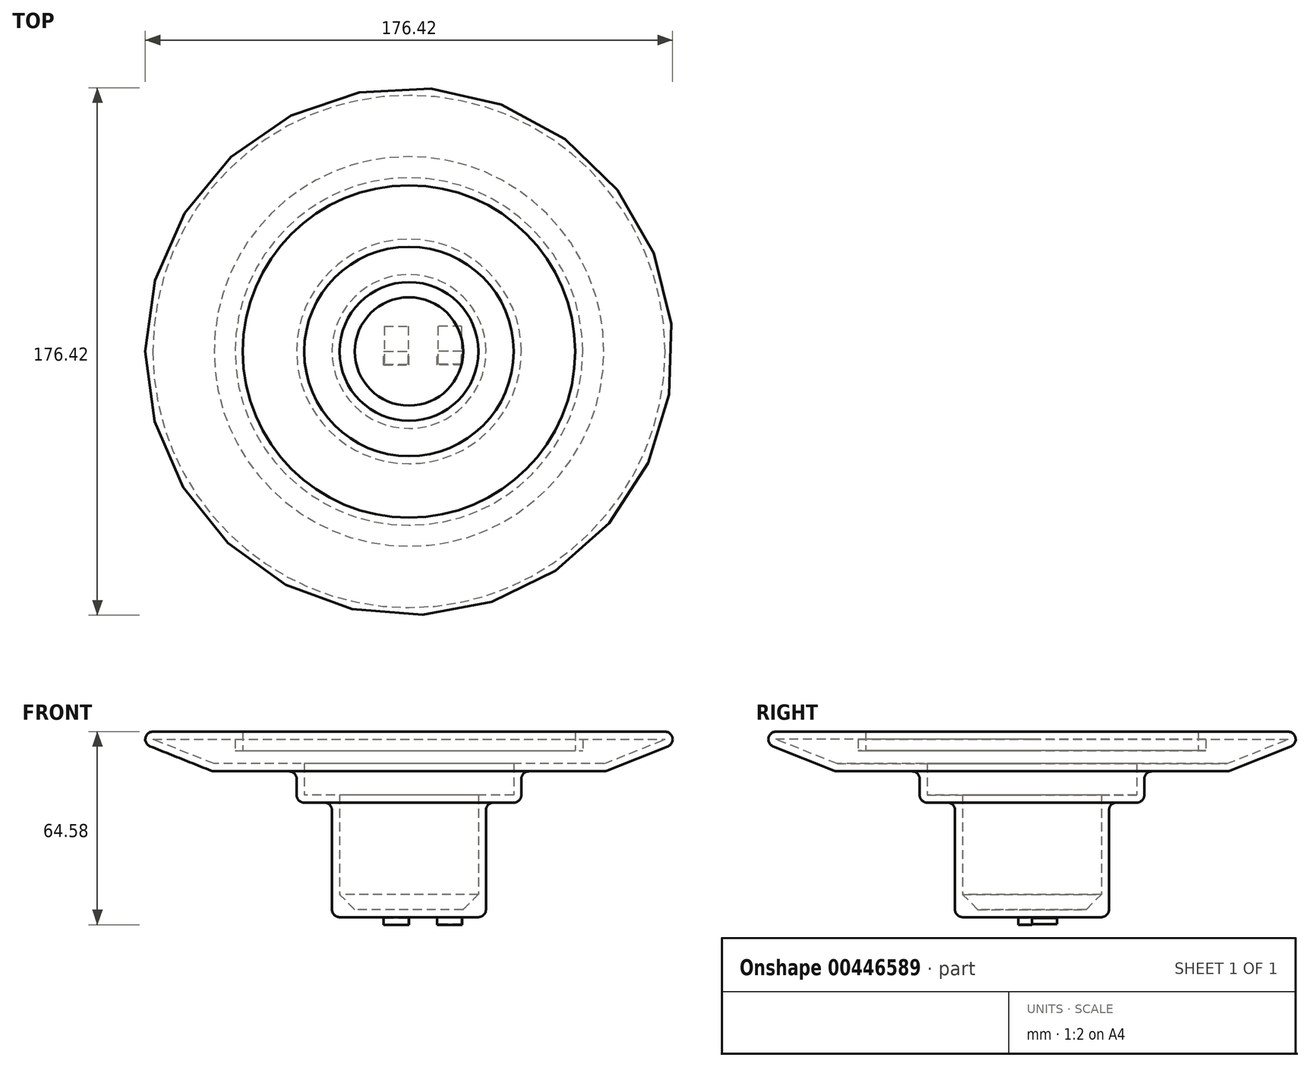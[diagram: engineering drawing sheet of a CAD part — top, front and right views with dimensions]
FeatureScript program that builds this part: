
annotation { "Feature Type Name" : "Feature", "Feature Type Description" : "" }
export const myFeature = defineFeature(function(context is Context, id is Id, definition is map)
    precondition{}
    {
        {
            var Q0;
            Q0=qCreatedBy(makeId("Right.planeOp"),FACE);
            var sketch = newSketch(context, id + "F0", { "sketchPlane" : qUnion([Q0])});
            skLineSegment(sketch, "E0", {"start": v(-118.44, 0) * mm, "end": v(120.69, 0) * mm, "construction": true});
            skLineSegment(sketch, "E1", {"start": v(0, -118.09) * mm, "end": v(0, 148.16) * mm, "construction": true});
            skLineSegment(sketch, "E2", {"start": v(-98.9, 0) * mm, "end": v(-65.67, -13.26) * mm});
            skLineSegment(sketch, "E3", {"start": v(-65.67, -13.26) * mm, "end": v(-37.58, -13.26) * mm});
            skLineSegment(sketch, "E4", {"start": v(-37.58, -13.26) * mm, "end": v(-37.58, -23.73) * mm});
            skLineSegment(sketch, "E5", {"start": v(-37.58, -23.73) * mm, "end": v(-25.75, -23.73) * mm});
            skLineSegment(sketch, "E6", {"start": v(-25.75, -23.73) * mm, "end": v(-25.75, -62.04) * mm});
            skLineSegment(sketch, "E7", {"start": v(-25.75, -62.04) * mm, "end": v(0, -62.04) * mm});
            skLineSegment(sketch, "E8", {"start": v(0, -62.04) * mm, "end": v(0, -6.3) * mm});
            skLineSegment(sketch, "E9", {"start": v(0, -6.3) * mm, "end": v(-55.6, -6.3) * mm});
            skLineSegment(sketch, "E10", {"start": v(-55.6, -6.3) * mm, "end": v(-55.6, 0) * mm});
            skLineSegment(sketch, "E11", {"start": v(-55.6, 0) * mm, "end": v(-98.9, 0) * mm});
            skSolve(sketch);
        }
        {
            var Q0;
            Q0=makeQuery(id+"F0.imprint","IMPRINT",FACE,{"disambiguationData":[TD([[makeQuery(id+"F0.imprint","IMPRINT",EDGE,{"derivedFrom":sQuery(id+"F0.wireOp",EDGE,"E2")}),1.0]])]});
            var Q1;
            Q1=sQuery(id+"F0.wireOp",EDGE,"E1");
            revolve(context, id + "F1", {"entities" : qUnion([Q0]), "axis" : qUnion([Q1]), "revolveType" : RevolveType.FULL});
        }
        {
            var Q0;
            Q0=makeQuery(id+"F1.opRevolve","SWEPT_FACE",FACE,{"disambiguationData":[OSD([sQuery(id+"F0.wireOp",EDGE,"E9")])]});
            shell(context, id + "F2", {"entities" : qUnion([Q0]), "thickness" : 2.54 * mm});
        }
        {
            var Q0;
            Q0=makeQuery(id+"F1.opRevolve","SWEPT_EDGE",EDGE,{"disambiguationData":[OSD([sQuery(id+"F0.wireOp",EDGE,"E6"),sQuery(id+"F0.wireOp",EDGE,"E7")])]});
            var Q1;
            Q1=makeQuery(id+"F1.opRevolve","SWEPT_EDGE",EDGE,{"disambiguationData":[OSD([sQuery(id+"F0.wireOp",EDGE,"E5"),sQuery(id+"F0.wireOp",EDGE,"E6")])]});
            var Q2;
            Q2=makeQuery(id+"F1.opRevolve","SWEPT_EDGE",EDGE,{"disambiguationData":[OSD([sQuery(id+"F0.wireOp",EDGE,"E3"),sQuery(id+"F0.wireOp",EDGE,"E4")])]});
            var Q3;
            Q3=makeQuery(id+"F1.opRevolve","SWEPT_EDGE",EDGE,{"disambiguationData":[OSD([sQuery(id+"F0.wireOp",EDGE,"E4"),sQuery(id+"F0.wireOp",EDGE,"E5")])]});
            var Q4;
            Q4=makeQuery(id+"F1.opRevolve","SWEPT_EDGE",EDGE,{"disambiguationData":[OSD([sQuery(id+"F0.wireOp",EDGE,"E2"),sQuery(id+"F0.wireOp",EDGE,"E3")])]});
            var Q5;
            Q5=makeQuery(id+"F1.opRevolve","SWEPT_EDGE",EDGE,{"disambiguationData":[OSD([sQuery(id+"F0.wireOp",EDGE,"E2"),sQuery(id+"F0.wireOp",EDGE,"E11")])]});
            fillet(context, id + "F3", {"entities" : qUnion([Q0, Q1, Q2, Q3, Q4, Q5]), "radius" : 2.54 * mm, "tangentPropagation" : true, "allowEdgeOverflow" : false});
        }
        {
            var Q0;
            Q0=makeQuery(id+"F2.opShell","OFFSET_EDGE",EDGE,{"disambiguationData":[OSD([sQuery(id+"F0.wireOp",EDGE,"E6"),sQuery(id+"F0.wireOp",EDGE,"E7")])]});
            chamfer(context, id + "F4", {"entities" : qUnion([Q0]), "width" : 5.08 * mm, "tangentPropagation" : true});
        }
        {
            var Q0;
            Q0=makeQuery(id+"F1.opRevolve","SWEPT_FACE",FACE,{"disambiguationData":[OSD([sQuery(id+"F0.wireOp",EDGE,"E7")])]});
            var sketch = newSketch(context, id + "F5", { "sketchPlane" : qUnion([Q0])});
            skLineSegment(sketch, "E12.bottom", {"start": v(-8.45, 4.55) * mm, "end": v(0, 4.55) * mm});
            skLineSegment(sketch, "E12.top", {"start": v(-8.45, 0) * mm, "end": v(0, 0) * mm});
            skLineSegment(sketch, "E12.left", {"start": v(-8.45, 4.55) * mm, "end": v(-8.45, 0) * mm});
            skLineSegment(sketch, "E12.right", {"start": v(0, 4.55) * mm, "end": v(0, 0) * mm});
            skLineSegment(sketch, "E13.MirrorCS", {"start": v(17.82, 4.55) * mm, "end": v(9.38, 4.55) * mm});
            skLineSegment(sketch, "E14.MirrorCS", {"start": v(9.38, 4.55) * mm, "end": v(9.38, 0) * mm});
            skLineSegment(sketch, "E15.MirrorCS", {"start": v(17.82, 0) * mm, "end": v(9.38, 0) * mm});
            skLineSegment(sketch, "E16.MirrorCS", {"start": v(17.82, 4.55) * mm, "end": v(17.82, 0) * mm});
            skSolve(sketch);
        }
        {
            var Q0;
            Q0=makeQuery(id+"F5.imprint","IMPRINT",FACE,{"disambiguationData":[TD([[makeQuery(id+"F5.imprint","IMPRINT",EDGE,{"derivedFrom":sQuery(id+"F5.wireOp",EDGE,"E13.MirrorCS")}),1.0]])]});
            var Q1;
            Q1=makeQuery(id+"F5.imprint","IMPRINT",FACE,{"disambiguationData":[TD([[makeQuery(id+"F5.imprint","IMPRINT",EDGE,{"derivedFrom":sQuery(id+"F5.wireOp",EDGE,"E12.bottom")}),-1.0]])]});
            extrude(context, id + "F6", {"entities" : qUnion([Q0, Q1]), "depth" : 2.54 * mm});
        }
        {
            var Q0;
            Q0=makeQuery(id+"F6.opExtrude","SWEPT_FACE",FACE,{"disambiguationData":[OSD([sQuery(id+"F5.wireOp",EDGE,"E12.top")])]});
            var Q1;
            Q1=makeQuery(id+"F6.opExtrude","SWEPT_FACE",FACE,{"disambiguationData":[OSD([sQuery(id+"F5.wireOp",EDGE,"E15.MirrorCS")])]});
            shell(context, id + "F7", {"entities" : qUnion([Q0, Q1]), "thickness" : 0.25 * mm});
        }
        {
            var Q0;
            Q0=makeQuery(id+"F7.opShell","OFFSET_FACE",FACE,{"disambiguationData":[OSD([sQuery(id+"F5.wireOp",EDGE,"E13.MirrorCS")])]});
            var Q1;
            Q1=makeQuery(id+"F7.opShell","OFFSET_FACE",FACE,{"disambiguationData":[OSD([sQuery(id+"F5.wireOp",EDGE,"E12.bottom")])]});
            extrude(context, id + "F8", {"entities" : qUnion([Q0, Q1]), "depth" : 12.7 * mm});
        }
    });
